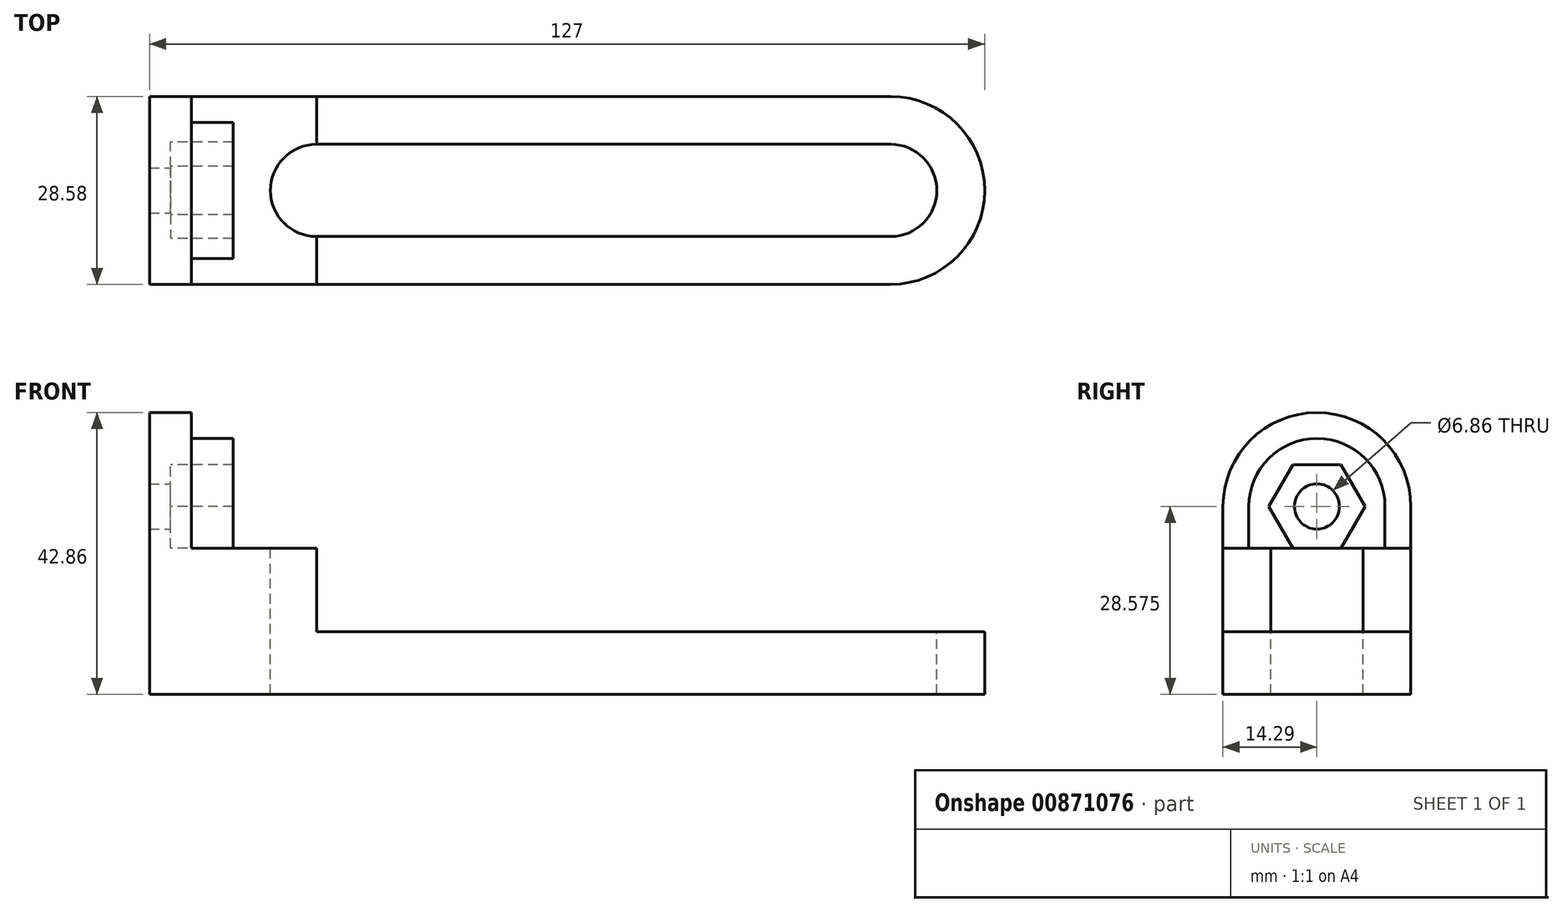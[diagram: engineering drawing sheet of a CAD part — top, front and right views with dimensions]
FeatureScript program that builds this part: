
annotation { "Feature Type Name" : "Feature", "Feature Type Description" : "" }
export const myFeature = defineFeature(function(context is Context, id is Id, definition is map)
    precondition{}
    {
        {
            var Q0;
            Q0=qCreatedBy(makeId("Top.planeOp"),FACE);
            var sketch = newSketch(context, id + "F0", { "sketchPlane" : qUnion([Q0])});
            skLineSegment(sketch, "E0.bottom", {"start": v(0, 14.29) * mm, "end": v(101.6, 14.29) * mm});
            skLineSegment(sketch, "E0.top", {"start": v(0, -14.29) * mm, "end": v(101.6, -14.29) * mm});
            skLineSegment(sketch, "E0.left", {"start": v(0, 14.29) * mm, "end": v(0, -14.29) * mm, "construction": true});
            skLineSegment(sketch, "E0.right", {"start": v(101.6, 14.29) * mm, "end": v(101.6, -14.29) * mm});
            skPoint(sketch, "E0.middle", {"position": v(50.8, 0) * mm});
            skLineSegment(sketch, "E1", {"start": v(0, 14.29) * mm, "end": v(-25.4, 14.29) * mm});
            skLineSegment(sketch, "E2", {"start": v(-25.4, 14.29) * mm, "end": v(-25.4, -14.29) * mm});
            skLineSegment(sketch, "E3", {"start": v(-25.4, -14.29) * mm, "end": v(0, -14.29) * mm});
            skSolve(sketch);
        }
        {
            var Q0;
            Q0 = qSketchRegion(id + "F0", true);
            extrude(context, id + "F1", {"entities" : qUnion([Q0]), "depth" : 9.52 * mm, "offsetDistance" : 25.4 * mm});
        }
        {
            var Q0;
            Q0=makeQuery(id+"F1.opExtrude","CAP_FACE",FACE,{"disambiguationData":[OSD([sQuery(id+"F0.wireOp",EDGE,"E0.bottom"),sQuery(id+"F0.wireOp",EDGE,"E0.top"),sQuery(id+"F0.wireOp",EDGE,"E0.right"),sQuery(id+"F0.wireOp",EDGE,"E1"),sQuery(id+"F0.wireOp",EDGE,"E2"),sQuery(id+"F0.wireOp",EDGE,"E3")])],"isStart":false});
            var sketch = newSketch(context, id + "F2", { "sketchPlane" : qUnion([Q0])});
            skLineSegment(sketch, "E4.bottom", {"start": v(-25.4, 14.29) * mm, "end": v(0, 14.29) * mm});
            skLineSegment(sketch, "E4.top", {"start": v(-25.4, -14.29) * mm, "end": v(0, -14.29) * mm});
            skLineSegment(sketch, "E4.left", {"start": v(-25.4, 14.29) * mm, "end": v(-25.4, -14.29) * mm});
            skLineSegment(sketch, "E4.right", {"start": v(0, 14.29) * mm, "end": v(0, -14.29) * mm});
            skSolve(sketch);
        }
        {
            var Q0;
            Q0 = qSketchRegion(id + "F2", true);
            extrude(context, id + "F3", {"entities" : qUnion([Q0]), "operationType" : NewBodyOperationType.ADD, "depth" : 12.7 * mm, "offsetDistance" : 25.4 * mm});
        }
        {
            var Q0;
            Q0=makeQuery(id+"F3.opExtrude","CAP_FACE",FACE,{"disambiguationData":[OSD([sQuery(id+"F2.wireOp",EDGE,"E4.bottom"),sQuery(id+"F2.wireOp",EDGE,"E4.top"),sQuery(id+"F2.wireOp",EDGE,"E4.left"),sQuery(id+"F2.wireOp",EDGE,"E4.right")])],"isStart":false});
            var sketch = newSketch(context, id + "F4", { "sketchPlane" : qUnion([Q0])});
            skLineSegment(sketch, "E5.bottom", {"start": v(-25.4, 14.29) * mm, "end": v(-19.05, 14.29) * mm});
            skLineSegment(sketch, "E5.top", {"start": v(-25.4, -14.29) * mm, "end": v(-19.05, -14.29) * mm});
            skLineSegment(sketch, "E5.left", {"start": v(-25.4, 14.29) * mm, "end": v(-25.4, -14.29) * mm});
            skLineSegment(sketch, "E5.right", {"start": v(-19.05, 14.29) * mm, "end": v(-19.05, -14.29) * mm});
            skSolve(sketch);
        }
        {
            var Q0;
            Q0 = qSketchRegion(id + "F4", true);
            extrude(context, id + "F5", {"entities" : qUnion([Q0]), "operationType" : NewBodyOperationType.ADD, "depth" : 25.4 * mm, "offsetDistance" : 25.4 * mm});
        }
        {
            var Q0;
            Q0=makeQuery(id+"F5.opExtrude","SWEPT_FACE",FACE,{"disambiguationData":[OSD([sQuery(id+"F4.wireOp",EDGE,"E5.right")])]});
            var sketch = newSketch(context, id + "F6", { "sketchPlane" : qUnion([Q0])});
            skCircle(sketch, "E6.cCircle", {"center": v(0, 28.58) * mm, "radius": 6.35 * mm, "construction": true});
            skLineSegment(sketch, "E6.0", {"start": v(3.67, 22.23) * mm, "end": v(-3.67, 22.23) * mm});
            skLineSegment(sketch, "E6.1", {"start": v(-3.67, 22.22) * mm, "end": v(-7.33, 28.57) * mm});
            skLineSegment(sketch, "E6.2", {"start": v(-7.33, 28.57) * mm, "end": v(-3.67, 34.93) * mm});
            skLineSegment(sketch, "E6.3", {"start": v(-3.67, 34.93) * mm, "end": v(3.67, 34.93) * mm});
            skLineSegment(sketch, "E6.4", {"start": v(3.67, 34.93) * mm, "end": v(7.33, 28.57) * mm});
            skLineSegment(sketch, "E6.5", {"start": v(7.33, 28.58) * mm, "end": v(3.67, 22.23) * mm});
            skPoint(sketch, "E6.0.midPoint", {"position": v(0, 22.23) * mm});
            skArc(sketch, "E7", {"start": v(10.35, 28.58) * mm, "mid": v(0, 38.93) * mm, "end": v(-10.35, 28.57) * mm});
            skLineSegment(sketch, "E8", {"start": v(-10.35, 28.57) * mm, "end": v(-10.35, 17.02) * mm});
            skLineSegment(sketch, "E9", {"start": v(-10.35, 17.02) * mm, "end": v(10.35, 17.02) * mm});
            skLineSegment(sketch, "E10", {"start": v(10.35, 17.02) * mm, "end": v(10.35, 28.58) * mm});
            skSolve(sketch);
        }
        {
            var Q0;
            Q0 = qSketchRegion(id + "F6", true);
            extrude(context, id + "F7", {"entities" : qUnion([Q0]), "operationType" : NewBodyOperationType.ADD, "depth" : 6.35 * mm, "offsetDistance" : 25.4 * mm});
        }
        {
            var Q0;
            {var subQ3=sQuery(id+"F6.wireOp",EDGE,"E7");Q0=makeQuery(id+"F6.imprint","IMPRINT",FACE,{"disambiguationData":[TD([[makeQuery(id+"F6.imprint","IMPRINT",EDGE,{"derivedFrom":subQ3}),-1.0]])]});}
            var sketch = newSketch(context, id + "F8", { "sketchPlane" : qUnion([Q0])});
            skArc(sketch, "E11", {"start": v(-14.29, 28.58) * mm, "mid": v(0, 42.86) * mm, "end": v(14.29, 28.58) * mm});
            skLineSegment(sketch, "E12", {"start": v(0, 28.58) * mm, "end": v(-14.29, 28.57) * mm, "construction": true});
            skLineSegment(sketch, "E13", {"start": v(0, 28.58) * mm, "end": v(14.29, 28.58) * mm, "construction": true});
            skCircle(sketch, "E14", {"center": v(0, 28.58) * mm, "radius": 3.43 * mm});
            skLineSegment(sketch, "E15", {"start": v(-14.29, 28.58) * mm, "end": v(-14.29, 47.62) * mm});
            skLineSegment(sketch, "E16", {"start": v(-14.29, 47.62) * mm, "end": v(14.29, 47.62) * mm});
            skLineSegment(sketch, "E17", {"start": v(14.29, 47.62) * mm, "end": v(14.29, 28.57) * mm});
            skSolve(sketch);
        }
        {
            var Q0;
            Q0 = qSketchRegion(id + "F8", true);
            extrude(context, id + "F9", {"entities" : qUnion([Q0]), "operationType" : NewBodyOperationType.REMOVE, "oppositeDirection" : true, "depth" : 25.4 * mm, "offsetDistance" : 25.4 * mm});
        }
        {
            var Q0;
            Q0=makeQuery(id+"F1.opExtrude","CAP_FACE",FACE,{"disambiguationData":[OSD([sQuery(id+"F0.wireOp",EDGE,"E0.bottom"),sQuery(id+"F0.wireOp",EDGE,"E0.top"),sQuery(id+"F0.wireOp",EDGE,"E0.right"),sQuery(id+"F0.wireOp",EDGE,"E1"),sQuery(id+"F0.wireOp",EDGE,"E2"),sQuery(id+"F0.wireOp",EDGE,"E3")])],"isStart":false});
            var sketch = newSketch(context, id + "F10", { "sketchPlane" : qUnion([Q0])});
            skArc(sketch, "E18", {"start": v(0, 7.01) * mm, "mid": v(-7.01, 0) * mm, "end": v(0, -7.01) * mm});
            skArc(sketch, "E19", {"start": v(87.31, -7.01) * mm, "mid": v(94.33, 0) * mm, "end": v(87.31, 7.01) * mm});
            skLineSegment(sketch, "E20", {"start": v(0, 7.01) * mm, "end": v(87.31, 7.01) * mm});
            skLineSegment(sketch, "E21", {"start": v(0, -7.01) * mm, "end": v(87.31, -7.01) * mm});
            skArc(sketch, "E22", {"start": v(87.31, 14.29) * mm, "mid": v(101.6, 0) * mm, "end": v(87.31, -14.29) * mm});
            skLineSegment(sketch, "E23", {"start": v(87.31, 14.29) * mm, "end": v(103.54, 14.29) * mm});
            skLineSegment(sketch, "E24", {"start": v(103.54, 14.29) * mm, "end": v(103.54, -17.25) * mm});
            skLineSegment(sketch, "E25", {"start": v(103.54, -17.25) * mm, "end": v(87.31, -14.29) * mm});
            skSolve(sketch);
        }
        {
            var Q0;
            Q0 = qSketchRegion(id + "F10", true);
            extrude(context, id + "F11", {"entities" : qUnion([Q0]), "operationType" : NewBodyOperationType.REMOVE, "oppositeDirection" : true, "depth" : 25.4 * mm, "offsetDistance" : 25.4 * mm, "hasSecondDirection" : true, "secondDirectionOppositeDirection" : false, "secondDirectionDepth" : 25.4 * mm});
        }
        {
            var Q0;
            Q0=makeQuery(id+"F6.imprint","IMPRINT",FACE,{"disambiguationData":[TD([[makeQuery(id+"F6.imprint","IMPRINT",EDGE,{"derivedFrom":sQuery(id+"F6.wireOp",EDGE,"E6.0")}),-1.0]])]});
            var sketch = newSketch(context, id + "F12", { "sketchPlane" : qUnion([Q0])});
            skLineSegment(sketch, "E26.0", {"start": v(7.33, 28.58) * mm, "end": v(3.67, 22.23) * mm});
            skLineSegment(sketch, "E27.0", {"start": v(3.67, 22.23) * mm, "end": v(-3.67, 22.23) * mm});
            skLineSegment(sketch, "E28.0", {"start": v(-3.67, 22.22) * mm, "end": v(-7.33, 28.57) * mm});
            skLineSegment(sketch, "E29.0", {"start": v(-7.33, 28.57) * mm, "end": v(-3.67, 34.93) * mm});
            skLineSegment(sketch, "E30.0", {"start": v(-3.67, 34.93) * mm, "end": v(3.67, 34.93) * mm});
            skLineSegment(sketch, "E31.0", {"start": v(3.67, 34.93) * mm, "end": v(7.33, 28.57) * mm});
            skSolve(sketch);
        }
        {
            var Q0;
            Q0 = qSketchRegion(id + "F12", true);
            extrude(context, id + "F13", {"entities" : qUnion([Q0]), "operationType" : NewBodyOperationType.REMOVE, "oppositeDirection" : true, "depth" : 3.17 * mm, "offsetDistance" : 25.4 * mm});
        }
    });
